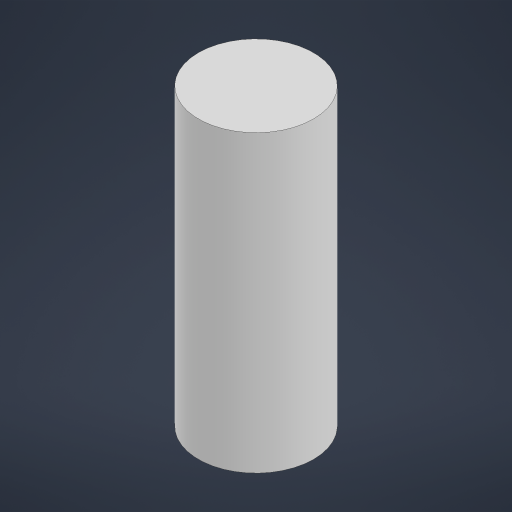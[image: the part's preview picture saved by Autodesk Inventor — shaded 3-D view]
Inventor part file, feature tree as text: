
AUTODESK INVENTOR PART (.ipt)
format: ipt  version: 2023 (Build 270158030, 158C)  size: 150,016 bytes
history: native  units: in
note: dims shown in document units (in); Inventor stores cm internally (conversion verified against a paired STEP export)
features: extrude x1, sketch x1
ambient origin geometry x8: Origin, YZ Plane, XZ Plane, XY Plane, X Axis, Y Axis, Z Axis, Center Point
bodies: Solid1 (feature_tree)
feature tree (2):
  extrude  "Extrusion1"  Depth=0.7874in TaperAngle=0.0deg
  sketch  "Sketch2"  dims[d0=0.3071in d1=0.7874in d2=0.0in]
